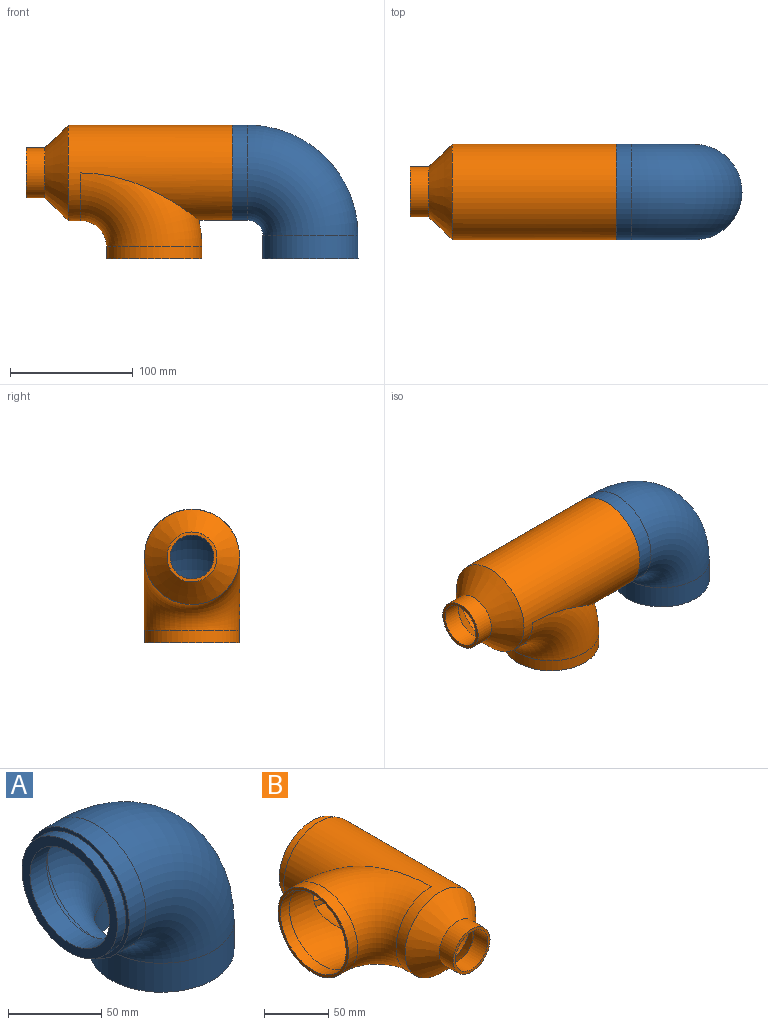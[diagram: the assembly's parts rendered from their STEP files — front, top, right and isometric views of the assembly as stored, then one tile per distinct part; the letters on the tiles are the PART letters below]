
ASSEMBLY  parts=2 mates=1
PART A: 12 faces, bbox 116x77.5x116 mm
  f0: cylinder r=36.2mm len=72.39mm, axis (-1,0,0), area 1444.1mm2, adj f2,f10
  f1: cylinder r=36.2mm len=72.39mm, axis (0,0,1), area 4332.3mm2, adj f2,f3
  f2: torus R=50.8mm, axis (0,-1,0), area 18156mm2, adj f0,f1
  f3: plane 77.47x77.47mm, normal (0,0,-1), area 597.9mm2, adj f1,f5
  f4: plane 77.47x77.47mm, normal (-1,0,0), area 597.9mm2, adj f7,f9
  f5: cylinder r=38.73mm len=77.47mm, axis (0,0,1), area 4636.4mm2, adj f3,f6
  f6: torus R=50.8mm, axis (0,-1,0), area 19430.1mm2, adj f5,f7
  f7: cylinder r=38.73mm len=77.48mm, axis (-1,0,0), area 3090.9mm2, adj f4,f6
  f8: cylinder r=30.16mm len=60.33mm, axis (-1,0,0), area 2406.9mm2, adj f10,f11
  f9: cylinder r=36.2mm len=72.39mm, axis (-1,0,0), area 1444.1mm2, adj f4,f11
  f10: plane 72.39x72.39mm, normal (1,0,0), area 1257.6mm2, adj f0,f8
  f11: plane 72.39x72.39mm, normal (-1,0,0), area 1257.6mm2, adj f8,f9
PART B: 17 faces, bbox 116.7x175.3x77.5 mm
  f0: cylinder r=36.2mm len=128.27mm, axis (0,1,0), area 21094.8mm2, adj f7,f11,f12
  f1: plane 77.47x77.47mm, normal (0,1,0), area 597.9mm2, adj f2,f8
  f2: cylinder r=38.73mm len=133.35mm, axis (0,1,0), area 23513.3mm2, adj f1,f5,f13
  f3: plane 77.47x77.47mm, normal (-1,0,0), area 597.9mm2, adj f4,f6
  f4: cylinder r=38.73mm len=77.47mm, axis (-1,0,0), area 2424mm2, adj f3,f5
  f5: torus R=59.89mm, axis (0,0,1), area 11386.5mm2, adj f2,f4
  f6: cylinder r=36.2mm len=72.39mm, axis (-1,0,0), area 2265mm2, adj f3,f7
  f7: torus R=59.89mm, axis (0,0,1), area 11139.7mm2, adj f0,f6
  f8: cylinder r=36.2mm len=72.39mm, axis (0,-1,0), area 1732.9mm2, adj f1,f10
  f9: cylinder r=30.73mm len=61.46mm, axis (0,-1,0), area 2452mm2, adj f10,f11
  f10: plane 72.39x72.39mm, normal (0,1,0), area 1149.4mm2, adj f8,f9
  f11: plane 72.39x72.39mm, normal (0,-1,0), area 1149.4mm2, adj f0,f9
  f12: cone r=17.78mm half-angle=44deg, axis (0,1,0), area 4492.8mm2, adj f0,f14
  f13: cone r=38.73mm half-angle=44deg, axis (0,1,0), area 4915.6mm2, adj f2,f15
  f14: cylinder r=17.78mm len=35.56mm, axis (0,1,0), area 1702.5mm2, adj f12,f16
  f15: cylinder r=20.32mm len=40.64mm, axis (0,1,0), area 1945.8mm2, adj f13,f16
  f16: plane 40.64x40.64mm, normal (0,-1,0), area 304mm2, adj f14,f15
PLACE A rot(axis=(0.08,-0.99,-0.08),0deg) t=(-78.48,-49.36,51.2)mm
PLACE B rot(axis=(-0.58,-0.58,-0.58),120deg) t=(-211.87,-49.36,120.94)mm
MATE slider B.f9 <-> A.f8  axis (1,0,0) through (-70.9,-49.36,121.05)mm
